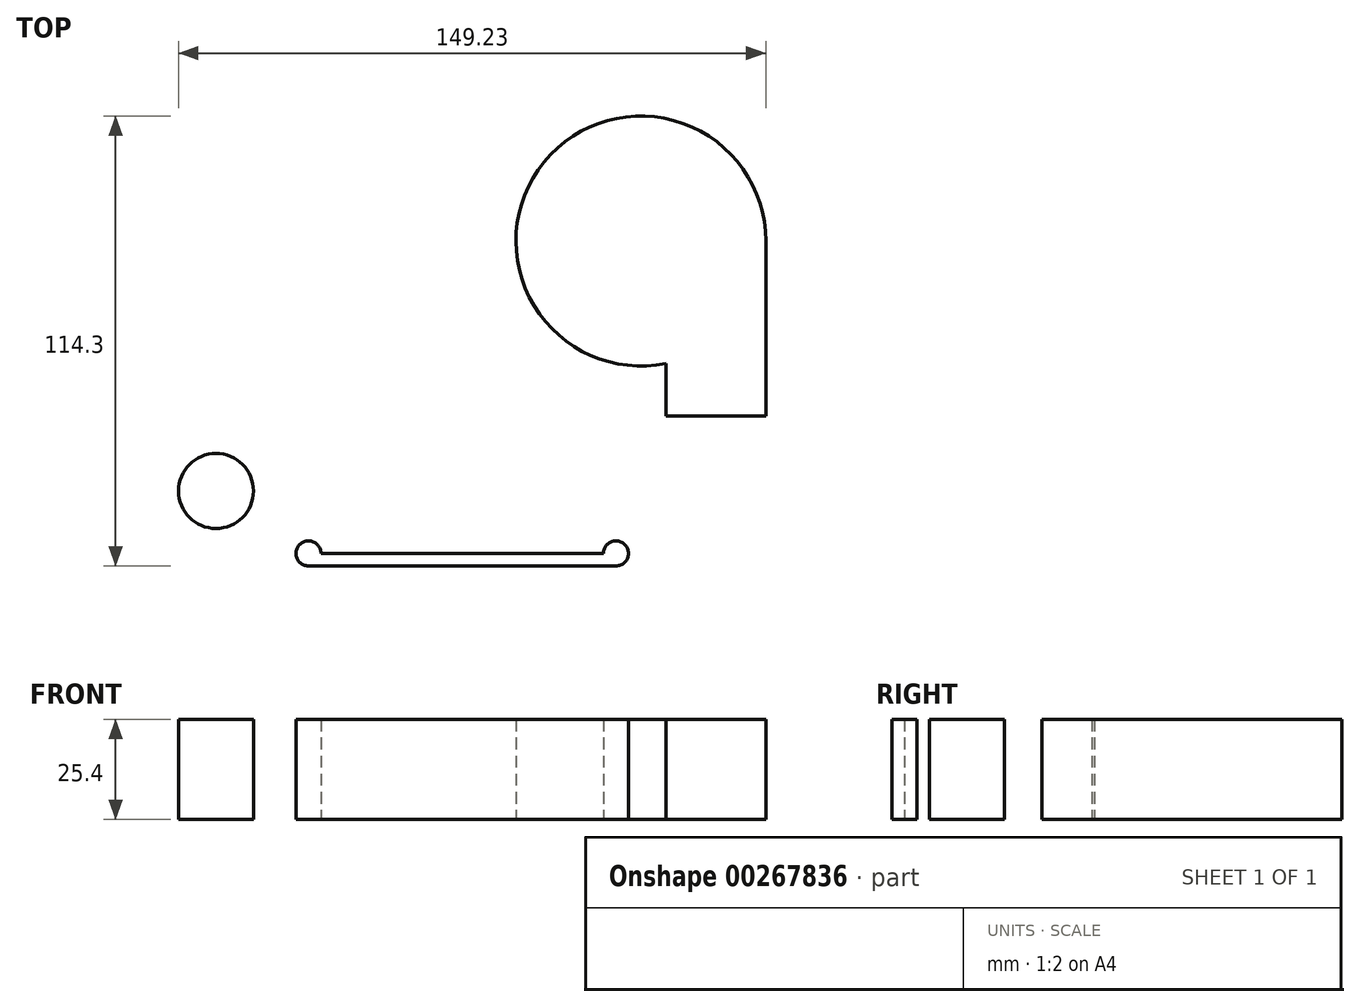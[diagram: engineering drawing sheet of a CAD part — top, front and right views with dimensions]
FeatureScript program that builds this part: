
annotation { "Feature Type Name" : "Feature", "Feature Type Description" : "" }
export const myFeature = defineFeature(function(context is Context, id is Id, definition is map)
    precondition{}
    {
        {
            var Q0;
            Q0=qCreatedBy(makeId("Top.planeOp"),FACE);
            var sketch = newSketch(context, id + "F0", { "sketchPlane" : qUnion([Q0])});
            skLineSegment(sketch, "E0", {"start": v(0, 0) * mm, "end": v(0, 25.4) * mm});
            skLineSegment(sketch, "E1", {"start": v(0, 0) * mm, "end": v(101.6, 0) * mm});
            skLineSegment(sketch, "E2", {"start": v(101.6, 0) * mm, "end": v(139.7, 0) * mm});
            skLineSegment(sketch, "E3", {"start": v(139.7, 0) * mm, "end": v(139.7, 44.45) * mm});
            skLineSegment(sketch, "E4", {"start": v(139.7, 44.45) * mm, "end": v(139.7, 76.2) * mm});
            skLineSegment(sketch, "E5", {"start": v(139.7, 76.2) * mm, "end": v(139.7, 82.55) * mm});
            skLineSegment(sketch, "E6", {"start": v(139.7, 82.55) * mm, "end": v(139.7, 88.9) * mm});
            skLineSegment(sketch, "E7", {"start": v(139.7, 88.9) * mm, "end": v(107.95, 88.9) * mm});
            skLineSegment(sketch, "E8", {"start": v(107.95, 88.9) * mm, "end": v(107.95, 120.65) * mm});
            skCircle(sketch, "E9", {"center": v(0, 25.4) * mm, "radius": 9.53 * mm});
            skCircle(sketch, "E10", {"center": v(107.95, 88.9) * mm, "radius": 31.75 * mm});
            skLineSegment(sketch, "E11", {"start": v(139.7, 82.55) * mm, "end": v(114.3, 82.55) * mm});
            skLineSegment(sketch, "E12", {"start": v(114.3, 82.55) * mm, "end": v(114.3, 44.45) * mm});
            skLineSegment(sketch, "E13", {"start": v(114.3, 44.45) * mm, "end": v(139.7, 44.45) * mm});
            skLineSegment(sketch, "E14", {"start": v(101.6, 0) * mm, "end": v(101.6, 6.35) * mm});
            skLineSegment(sketch, "E15", {"start": v(101.6, 6.35) * mm, "end": v(16.8, 6.35) * mm});
            skLineSegment(sketch, "E16", {"start": v(101.6, 6.35) * mm, "end": v(101.6, 9.53) * mm});
            skCircle(sketch, "E17", {"center": v(101.6, 9.53) * mm, "radius": 3.18 * mm});
            skLineSegment(sketch, "E18", {"start": v(101.6, 9.53) * mm, "end": v(19.83, 9.53) * mm});
            skLineSegment(sketch, "E19", {"start": v(21.65, 12.12) * mm, "end": v(38.86, 12.12) * mm});
            skLineSegment(sketch, "E20", {"start": v(21.65, 12.12) * mm, "end": v(21.65, 7.86) * mm});
            skCircle(sketch, "E21.MirrorC", {"center": v(23.48, 9.53) * mm, "radius": 3.18 * mm});
            skLineSegment(sketch, "E22", {"start": v(21.65, 12.12) * mm, "end": v(20.39, 10.25) * mm});
            skLineSegment(sketch, "E23", {"start": v(21.02, 11.19) * mm, "end": v(19.7, 12.08) * mm});
            skSolve(sketch);
        }
        {
            var Q0;
            Q0 = qSketchRegion(id + "F0", true);
            extrude(context, id + "F1", {"entities" : qUnion([Q0]), "depth" : 25.4 * mm});
        }
    });
